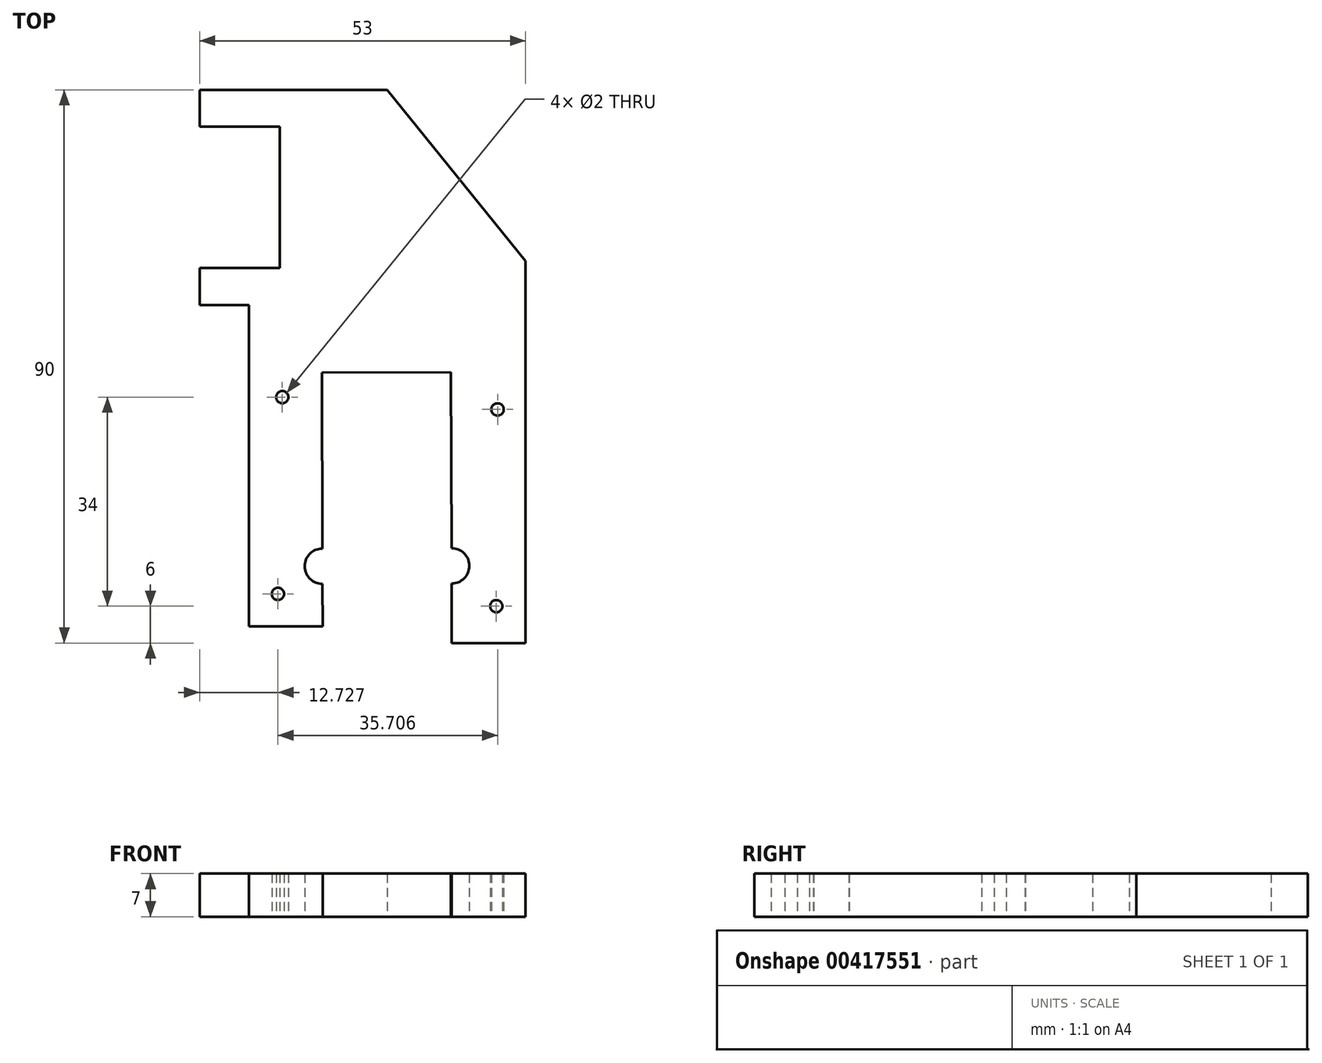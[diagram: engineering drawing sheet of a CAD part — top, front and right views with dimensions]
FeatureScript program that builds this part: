
annotation { "Feature Type Name" : "Feature", "Feature Type Description" : "" }
export const myFeature = defineFeature(function(context is Context, id is Id, definition is map)
    precondition{}
    {
        {
            var Q0;
            Q0=qCreatedBy(makeId("Top.planeOp"),FACE);
            var sketch = newSketch(context, id + "F0", { "sketchPlane" : qUnion([Q0])});
            skLineSegment(sketch, "E0.bottom", {"start": v(22.5, -45) * mm, "end": v(10.5, -45) * mm});
            skLineSegment(sketch, "E0.top", {"start": v(22.5, 45) * mm, "end": v(-22.5, 45) * mm});
            skLineSegment(sketch, "E0.left", {"start": v(22.5, -45) * mm, "end": v(22.5, 45) * mm});
            skLineSegment(sketch, "E0.right", {"start": v(-22.5, -42.25) * mm, "end": v(-22.5, 45) * mm});
            skPoint(sketch, "E0.middle", {"position": v(0, 0) * mm});
            skLineSegment(sketch, "E1.bottom", {"start": v(-10.63, -1) * mm, "end": v(10.37, -0.94) * mm});
            skLineSegment(sketch, "E1.left", {"start": v(-10.63, -1) * mm, "end": v(-10.5, -42.25) * mm});
            skLineSegment(sketch, "E1.right", {"start": v(10.37, -0.94) * mm, "end": v(10.5, -45) * mm});
            skLineSegment(sketch, "E2.bottom", {"start": v(-22.5, 39) * mm, "end": v(-14.5, 39) * mm});
            skLineSegment(sketch, "E2.top", {"start": v(-22.5, 45) * mm, "end": v(-14.5, 45) * mm});
            skLineSegment(sketch, "E2.left", {"start": v(-22.5, 39) * mm, "end": v(-22.5, 45) * mm});
            skLineSegment(sketch, "E2.right", {"start": v(-14.5, 39) * mm, "end": v(-14.5, 45) * mm});
            skLineSegment(sketch, "E3.bottom", {"start": v(-22.5, 16) * mm, "end": v(-14.5, 16) * mm});
            skLineSegment(sketch, "E3.top", {"start": v(-22.5, 10) * mm, "end": v(-14.5, 10) * mm});
            skLineSegment(sketch, "E3.left", {"start": v(-22.5, 16) * mm, "end": v(-22.5, 10) * mm});
            skLineSegment(sketch, "E3.right", {"start": v(-14.5, 16) * mm, "end": v(-14.5, 10) * mm});
            skPoint(sketch, "E4", {"position": v(-17.77, -37) * mm});
            skPoint(sketch, "E5", {"position": v(-17.07, -5) * mm});
            skPoint(sketch, "E6", {"position": v(17.93, -7) * mm});
            skPoint(sketch, "E7", {"position": v(17.73, -39) * mm});
            skPoint(sketch, "E8.positionSnap0", {"position": v(-18.5, 45) * mm});
            skPoint(sketch, "E9.positionSnap0", {"position": v(-18.5, 16) * mm});
            skPoint(sketch, "E10", {"position": v(-10.54, -32.5) * mm});
            skPoint(sketch, "E11", {"position": v(0, 45) * mm});
            skPoint(sketch, "E12", {"position": v(22.5, 17.15) * mm});
            skLineSegment(sketch, "E13", {"start": v(0, 45) * mm, "end": v(22.5, 17.15) * mm});
            skPoint(sketch, "E14", {"position": v(10.46, -32.44) * mm});
            skLineSegment(sketch, "E15", {"start": v(0, -64.42) * mm, "end": v(0, 71.46) * mm, "construction": true});
            skPoint(sketch, "E16", {"position": v(-22.5, -39) * mm});
            skPoint(sketch, "E17", {"position": v(-22.5, -42.25) * mm});
            skLineSegment(sketch, "E18", {"start": v(-22.5, -42.25) * mm, "end": v(-10.5, -42.25) * mm});
            skPoint(sketch, "E19.trimOffspring.end.orphan", {"position": v(-22.5, -45) * mm});
            skSolve(sketch);
        }
        {
            var Q0;
            Q0=makeQuery(id+"F0.imprint","IMPRINT",FACE,{"disambiguationData":[TD([[makeQuery(id+"F0.imprint","IMPRINT",EDGE,{"derivedFrom":sQuery(id+"F0.wireOp",EDGE,"E0.bottom")}),-1.0]])]});
            extrude(context, id + "F1", {"entities" : qUnion([Q0]), "depth" : 7 * mm});
        }
        {
            var Q0;
            Q0=sQuery(id+"F0.wireOp",VERTEX,"E5");
            var Q1;
            Q1=sQuery(id+"F0.wireOp",VERTEX,"E4");
            var Q2;
            Q2=sQuery(id+"F0.wireOp",VERTEX,"E7");
            var Q3;
            Q3=sQuery(id+"F0.wireOp",VERTEX,"E6");
            var Q4;
            Q4=makeQuery(id+"F1.opExtrude","SWEPT_BODY",BODY,{"disambiguationData":[OSD([sQuery(id+"F0.wireOp",EDGE,"E0.bottom"),sQuery(id+"F0.wireOp",EDGE,"E0.top"),sQuery(id+"F0.wireOp",EDGE,"E0.left"),sQuery(id+"F0.wireOp",EDGE,"E0.right"),sQuery(id+"F0.wireOp",EDGE,"E1.bottom"),sQuery(id+"F0.wireOp",EDGE,"E1.left"),sQuery(id+"F0.wireOp",EDGE,"E1.right"),sQuery(id+"F0.wireOp",EDGE,"E2.bottom"),sQuery(id+"F0.wireOp",EDGE,"E2.right"),sQuery(id+"F0.wireOp",EDGE,"E3.bottom"),sQuery(id+"F0.wireOp",EDGE,"E3.top"),sQuery(id+"F0.wireOp",EDGE,"E3.right"),sQuery(id+"F0.wireOp",EDGE,"E19.trimOffspring")])]});
            hole(context, id + "F2", {"style" : HoleStyle.SIMPLE, "endStyle" : HoleEndStyle.THROUGH, "oppositeDirection" : true, "holeDiameter" : 2 * mm, "isTappedThrough" : true, "tappedDepth" : 12.7 * mm, "tapClearance" : 3, "locations" : qUnion([Q0, Q1, Q2, Q3]), "scope" : qUnion([Q4])});
        }
        {
            var Q0;
            Q0=sQuery(id+"F0.wireOp",VERTEX,"E10");
            var Q1;
            Q1=sQuery(id+"F0.wireOp",VERTEX,"E14");
            var Q2;
            Q2=makeQuery(id+"F1.opExtrude","SWEPT_BODY",BODY,{"disambiguationData":[OSD([sQuery(id+"F0.wireOp",EDGE,"E0.bottom"),sQuery(id+"F0.wireOp",EDGE,"E0.top"),sQuery(id+"F0.wireOp",EDGE,"E0.left"),sQuery(id+"F0.wireOp",EDGE,"E0.right"),sQuery(id+"F0.wireOp",EDGE,"E1.bottom"),sQuery(id+"F0.wireOp",EDGE,"E1.left"),sQuery(id+"F0.wireOp",EDGE,"E1.right"),sQuery(id+"F0.wireOp",EDGE,"E2.bottom"),sQuery(id+"F0.wireOp",EDGE,"E2.right"),sQuery(id+"F0.wireOp",EDGE,"E3.bottom"),sQuery(id+"F0.wireOp",EDGE,"E3.top"),sQuery(id+"F0.wireOp",EDGE,"E3.right"),sQuery(id+"F0.wireOp",EDGE,"E19.trimOffspring")])]});
            hole(context, id + "F3", {"style" : HoleStyle.SIMPLE, "endStyle" : HoleEndStyle.THROUGH, "oppositeDirection" : true, "holeDiameter" : 5.75 * mm, "isTappedThrough" : true, "tappedDepth" : 12.7 * mm, "tapClearance" : 3, "locations" : qUnion([Q0, Q1]), "scope" : qUnion([Q2])});
        }
        {
            var Q0;
            Q0=makeQuery(id+"F1.opExtrude","SWEPT_FACE",FACE,{"disambiguationData":[OSD([sQuery(id+"F0.wireOp",EDGE,"E2.right")])]});
            var Q1;
            Q1=makeQuery(id+"F1.opExtrude","SWEPT_FACE",FACE,{"disambiguationData":[OSD([sQuery(id+"F0.wireOp",EDGE,"E3.right")])]});
            extrude(context, id + "F4", {"entities" : qUnion([Q0, Q1]), "operationType" : NewBodyOperationType.ADD, "depth" : 16 * mm});
        }
        {
            var Q0;
            {var subQ0=sQuery(id+"F0.wireOp",EDGE,"E0.right");Q0=makeQuery(id+"F1.opExtrude","SWEPT_FACE",FACE,{"disambiguationData":[OSD([subQ0]),TDD([makeQuery(id+"F0.imprint","IMPRINT",EDGE,{"disambiguationData":[TD([[makeQuery(id+"F0.imprint","INTERSECT",VERTEX,{"derivedFrom":[subQ0,sQuery(id+"F0.wireOp",EDGE,"E2.bottom"),sQuery(id+"F0.wireOp",EDGE,"E2.left")]}),1.0]])],"derivedFrom":subQ0})])]});}
            extrude(context, id + "F5", {"entities" : qUnion([Q0]), "operationType" : NewBodyOperationType.REMOVE, "oppositeDirection" : true, "depth" : 5 * mm});
        }
    });
